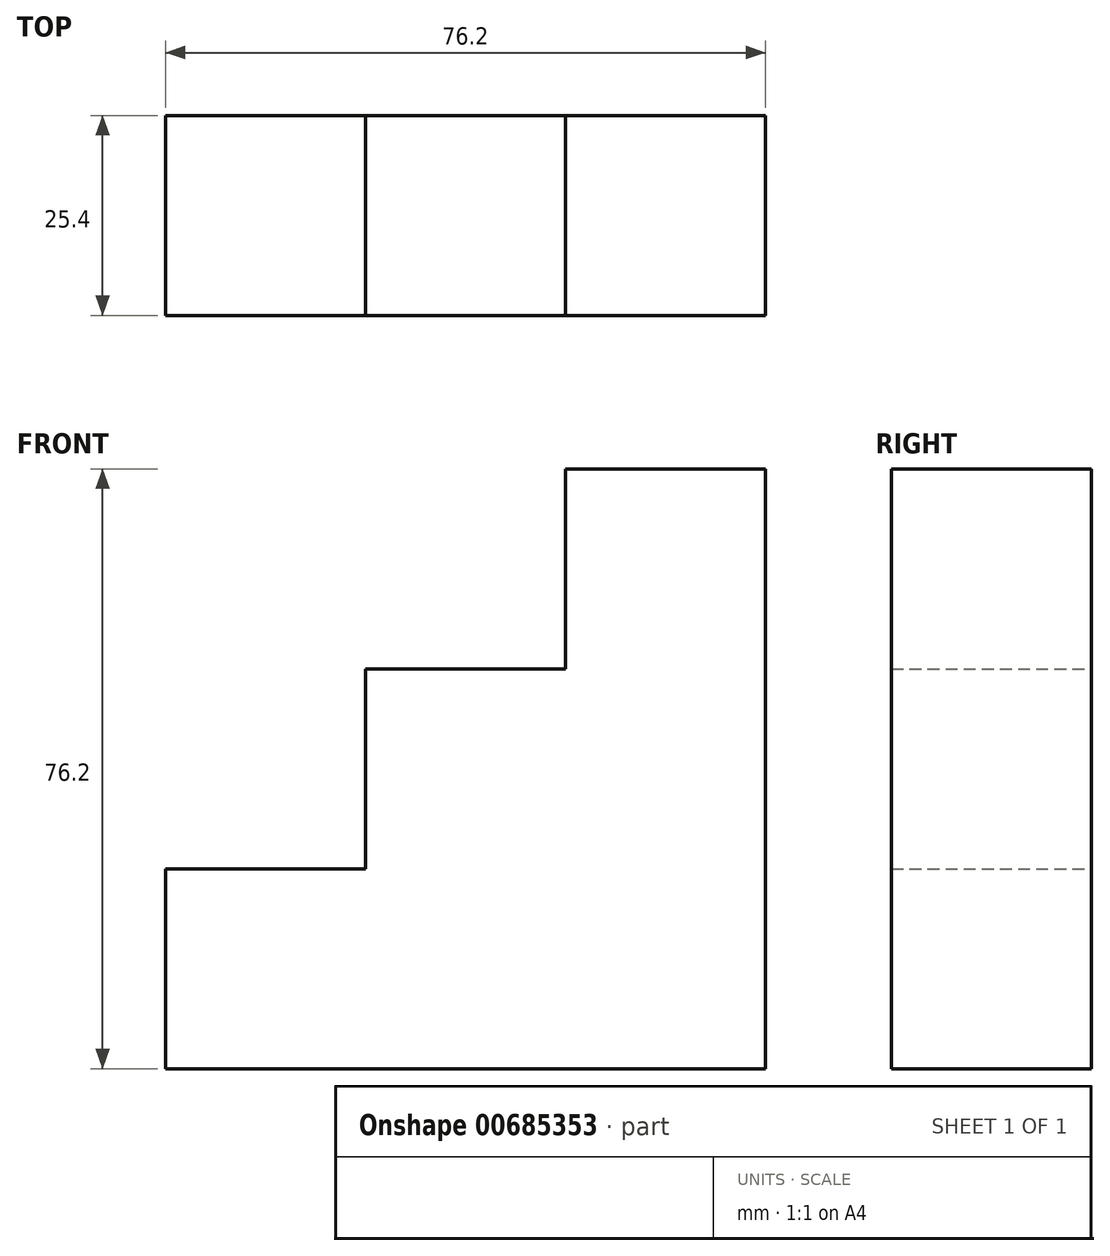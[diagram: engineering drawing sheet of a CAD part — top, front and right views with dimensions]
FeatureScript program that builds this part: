
annotation { "Feature Type Name" : "Feature", "Feature Type Description" : "" }
export const myFeature = defineFeature(function(context is Context, id is Id, definition is map)
    precondition{}
    {
        {
            var Q0;
            Q0=qCreatedBy(makeId("Front.planeOp"),FACE);
            var sketch = newSketch(context, id + "F0", { "sketchPlane" : qUnion([Q0])});
            skLineSegment(sketch, "E0", {"start": v(-38.51, -17.6) * mm, "end": v(37.69, -17.6) * mm});
            skLineSegment(sketch, "E1", {"start": v(-38.51, -17.6) * mm, "end": v(-38.51, 7.8) * mm});
            skLineSegment(sketch, "E2", {"start": v(37.69, -17.6) * mm, "end": v(37.69, 58.6) * mm});
            skLineSegment(sketch, "E3", {"start": v(-38.51, 7.8) * mm, "end": v(-13.11, 7.8) * mm});
            skLineSegment(sketch, "E4", {"start": v(-13.11, 7.8) * mm, "end": v(-13.11, 33.2) * mm});
            skLineSegment(sketch, "E5", {"start": v(-13.11, 33.2) * mm, "end": v(12.29, 33.2) * mm});
            skLineSegment(sketch, "E6", {"start": v(12.29, 33.2) * mm, "end": v(12.29, 58.6) * mm});
            skLineSegment(sketch, "E7", {"start": v(12.29, 58.6) * mm, "end": v(37.69, 58.6) * mm});
            skSolve(sketch);
        }
        {
            var Q0;
            Q0=makeQuery(id+"F0.imprint","IMPRINT",FACE,{"disambiguationData":[TD([[makeQuery(id+"F0.imprint","IMPRINT",EDGE,{"derivedFrom":sQuery(id+"F0.wireOp",EDGE,"E0")}),1.0]])]});
            extrude(context, id + "F1", {"entities" : qUnion([Q0]), "depth" : 25.4 * mm, "offsetDistance" : 25.4 * mm});
        }
    });
